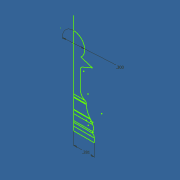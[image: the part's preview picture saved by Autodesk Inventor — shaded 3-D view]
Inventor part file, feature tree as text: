
AUTODESK INVENTOR PART (.ipt)
format: ipt  version: 2018 (Build 220112000, 112)  size: 84,992 bytes
history: native  units: in
note: dims shown in document units (in); Inventor stores cm internally (conversion verified against a paired STEP export)
features: sketch x1
ambient origin geometry x8: Origin, YZ Plane, XZ Plane, XY Plane, X Axis, Y Axis, Z Axis, Center Point
feature tree (1):
  sketch  "Sketch1"  dims[d1=0.3in d2=0.1in d3=0.2807in]
